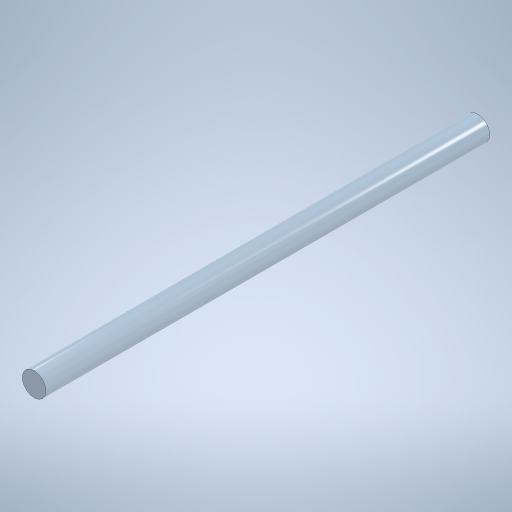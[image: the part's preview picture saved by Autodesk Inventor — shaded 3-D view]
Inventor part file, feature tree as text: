
AUTODESK INVENTOR PART (.ipt)
format: ipt  version: 2023.1 (Build 271208000, 208)  size: 239,616 bytes
history: native  units: mm
features: extrude x1, sketch x1
ambient origin geometry x8: Origin, YZ Plane, XZ Plane, XY Plane, X Axis, Y Axis, Z Axis, Center Point
bodies: Solid1 (feature_tree)
feature tree (2):
  extrude  "Extrusion1"  Depth=150.0mm TaperAngle=0.0deg
  sketch  "Sketch1"  dims[d0=8.0mm d1=150.0mm d2=0.0mm]
